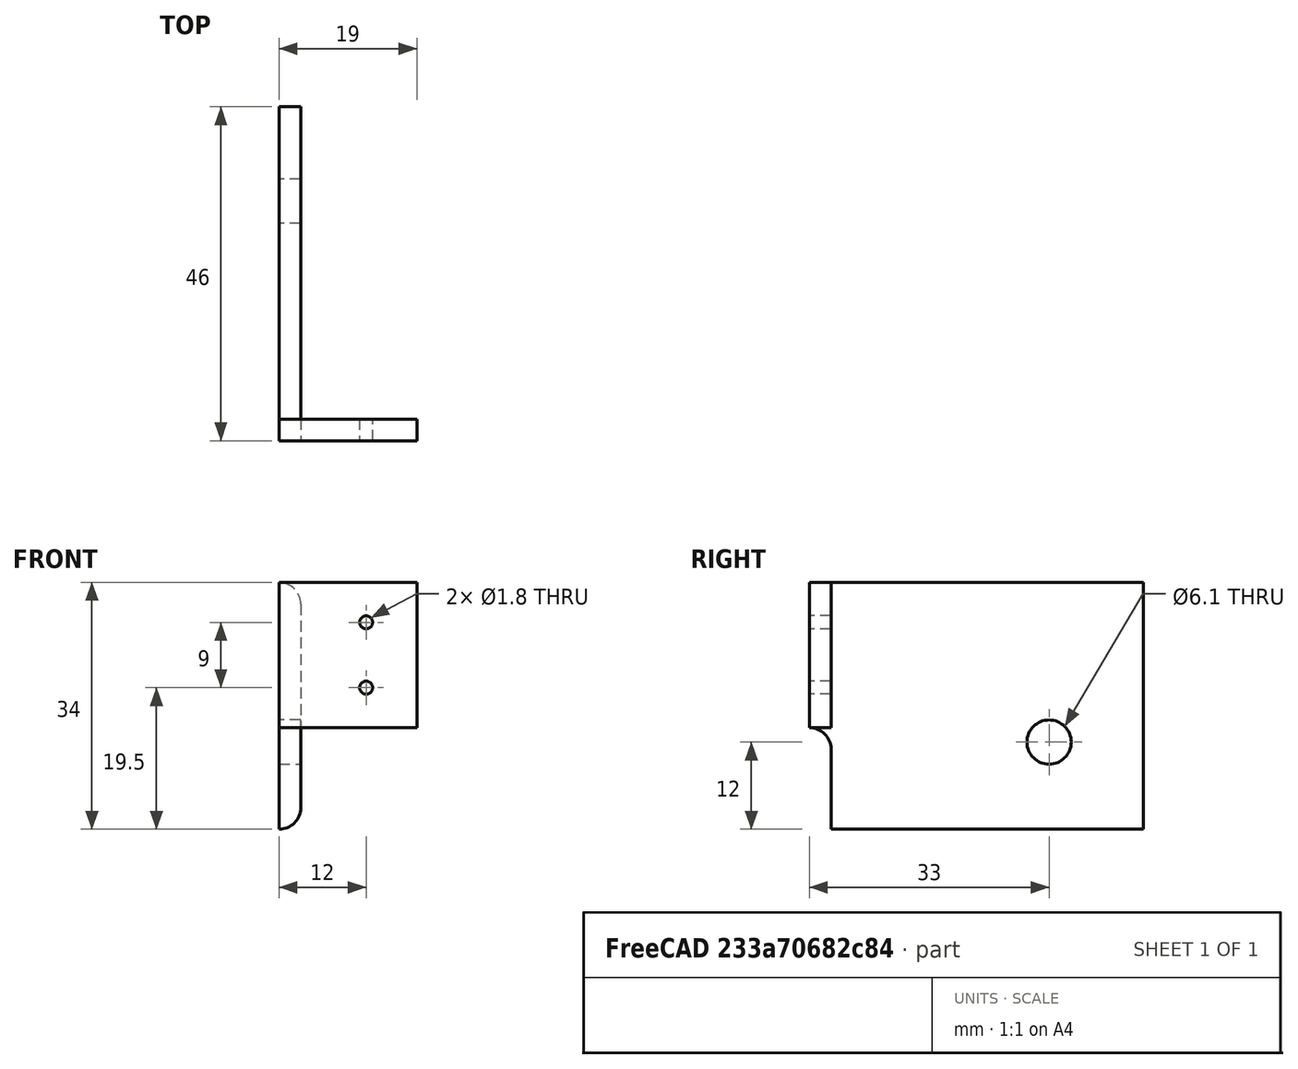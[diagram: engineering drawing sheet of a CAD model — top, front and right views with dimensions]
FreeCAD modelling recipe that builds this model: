
FCSTD DOCUMENT  (FreeCAD 0.21R33771 (Git))
Label: y_end_stop
License: All rights reserved
LicenseURL: https://en.wikipedia.org/wiki/All_rights_reserved
objects: Sketcher::SketchObject×4, PartDesign::Pad×2, PartDesign::Fillet×2, PartDesign::Pocket×2, PartDesign::Body×1, Mesh::Feature×1
note: 17 computed .brp shape members not serialized (recipe doc carries the construction recipe); baked Part::Feature solids carry a one-line shape summary decoded from their .brp

FEATURE [Sketcher::SketchObject] Sketch
  FullyConstrained = true
  MapMode = 5
  Placement = pos=(0,0,0) rot=(1,0,0;1.5708rad)
  Support = -> [XZ_Plane]
  sketch-geometry (4):
    g0: LineSegment StartX=0 StartY=34 StartZ=0 EndX=3 EndY=34 EndZ=0
    g1: LineSegment StartX=3 StartY=34 StartZ=0 EndX=3 EndY=0 EndZ=0
    g2: LineSegment StartX=3 StartY=0 StartZ=0 EndX=0 EndY=0 EndZ=0
    g3: LineSegment StartX=0 StartY=0 StartZ=0 EndX=0 EndY=34 EndZ=0
  constraints (11):
    c: Coincident(g0,g1)
    c: Coincident(g1,g2)
    c: Coincident(g2,g3)
    c: Coincident(g3,g0)
    c: Horizontal(g0)
    c: Horizontal(g2)
    c: Vertical(g1)
    c: Vertical(g3)
    c: DistanceY(g1,g1) = 34
    c: DistanceX(g0,g0) = 3
    c: Coincident(g2,g-1)
FEATURE [PartDesign::Pad] Pad
  Direction = (0,-1,2e-16)
  Length = 43
  Length2 = 10
  Placement = pos=(0,0,0) rot=(1,0,0;1.5708rad)
  Profile = -> Sketch
  ReferenceAxis = -> Sketch [N_Axis]
  Type = 0
FEATURE [PartDesign::Fillet] Fillet
  Base = -> Pad [Edge5,Edge2]
  BaseFeature = -> Pad
  Placement = pos=(0,0,0) rot=(1,0,0;1.5708rad)
  Radius = 2.99
  SupportTransform = false
  UseAllEdges = false
FEATURE [Sketcher::SketchObject] Sketch001
  ExternalGeometry = -> [Fillet]
  FullyConstrained = true
  MapMode = 5
  Placement = pos=(0,-43,0) rot=(1,0,0;1.5708rad)
  Support = -> [Fillet]
  sketch-geometry (4):
    g0: LineSegment StartX=0 StartY=34 StartZ=0 EndX=19 EndY=34 EndZ=0
    g1: LineSegment StartX=19 StartY=34 StartZ=0 EndX=19 EndY=14 EndZ=0
    g2: LineSegment StartX=19 StartY=14 StartZ=0 EndX=0 EndY=14 EndZ=0
    g3: LineSegment StartX=0 StartY=14 StartZ=0 EndX=0 EndY=34 EndZ=0
  constraints (11):
    c: Coincident(g0,g1)
    c: Coincident(g1,g2)
    c: Coincident(g2,g3)
    c: Coincident(g3,g0)
    c: Horizontal(g0)
    c: Horizontal(g2)
    c: Vertical(g1)
    c: Vertical(g3)
    c: Coincident(g0,g-3)
    c: DistanceX(g0,g0) = 19
    c: DistanceY(g1,g1) = 20
FEATURE [PartDesign::Pad] Pad001
  BaseFeature = -> Fillet
  Direction = (0,-1,2e-16)
  Length = 3
  Length2 = 10
  Placement = pos=(0,0,0) rot=(1,0,0;1.5708rad)
  Profile = -> Sketch001
  ReferenceAxis = -> Sketch001 [N_Axis]
  Type = 0
FEATURE [Sketcher::SketchObject] Sketch002
  ExternalGeometry = -> [Pad001]
  FullyConstrained = true
  MapMode = 5
  Placement = pos=(0,-46,1.63e-14) rot=(1,0,0;1.5708rad)
  Support = -> [Pad001]
  sketch-geometry (2):
    g0: Circle CenterX=12 CenterY=28.5 CenterZ=0 NormalX=0 NormalY=0 NormalZ=1 AngleXU=0 Radius=0.9
    g1: Circle CenterX=12 CenterY=19.5 CenterZ=0 NormalX=0 NormalY=0 NormalZ=1 AngleXU=0 Radius=0.9
  constraints (6):
    c: Vertical(g1,g0)
    c: Equal(g0,g1)
    c: Diameter(g0) = 1.8
    c: DistanceY(g1,g0) = 9
    c: DistanceX(g0,g-3) = 7
    c: DistanceY(g0,g-3) = 5.5
FEATURE [PartDesign::Pocket] Pocket
  BaseFeature = -> Pad001
  Direction = (0,1,-4e-16)
  Length = 5
  Length2 = 5
  Placement = pos=(0,0,0) rot=(1,0,0;1.5708rad)
  Profile = -> Sketch002
  ReferenceAxis = -> Sketch002 [N_Axis]
  Type = 1
FEATURE [Sketcher::SketchObject] Sketch003
  ExternalGeometry = -> [Pocket]
  FullyConstrained = true
  MapMode = 5
  Placement = pos=(0,0,0) rot=(0.707107,0,-0.707107;3.14159rad)
  Support = -> [Pocket]
  sketch-geometry (1):
    g0: Circle CenterX=-12 CenterY=13 CenterZ=0 NormalX=0 NormalY=0 NormalZ=1 AngleXU=0 Radius=3.05
  constraints (3):
    c: Diameter(g0) = 6.1
    c: DistanceX(g0,g-3) = 12
    c: DistanceY(g0,g-3) = 30
FEATURE [PartDesign::Pocket] Pocket001
  BaseFeature = -> Pocket
  Direction = (1,0,2e-16)
  Length = 5
  Length2 = 5
  Placement = pos=(0,0,0) rot=(1,0,0;1.5708rad)
  Profile = -> Sketch003
  ReferenceAxis = -> Sketch003 [N_Axis]
  Type = 1
FEATURE [PartDesign::Fillet] Fillet001
  Base = -> Pocket001 [Edge31]
  BaseFeature = -> Pocket001
  Placement = pos=(0,0,0) rot=(1,0,0;1.5708rad)
  Radius = 2.99
  SupportTransform = false
  UseAllEdges = false
FEATURE [PartDesign::Body] Body
  Group = -> [Sketch,Pad,Fillet,Sketch001,Pad001,Sketch002,Pocket,Sketch003,Pocket001,Fillet001]
  Origin = -> Origin
  Tip = -> Fillet001
FEATURE [Mesh::Feature] Mesh  label="Fillet001 (Meshed)"
